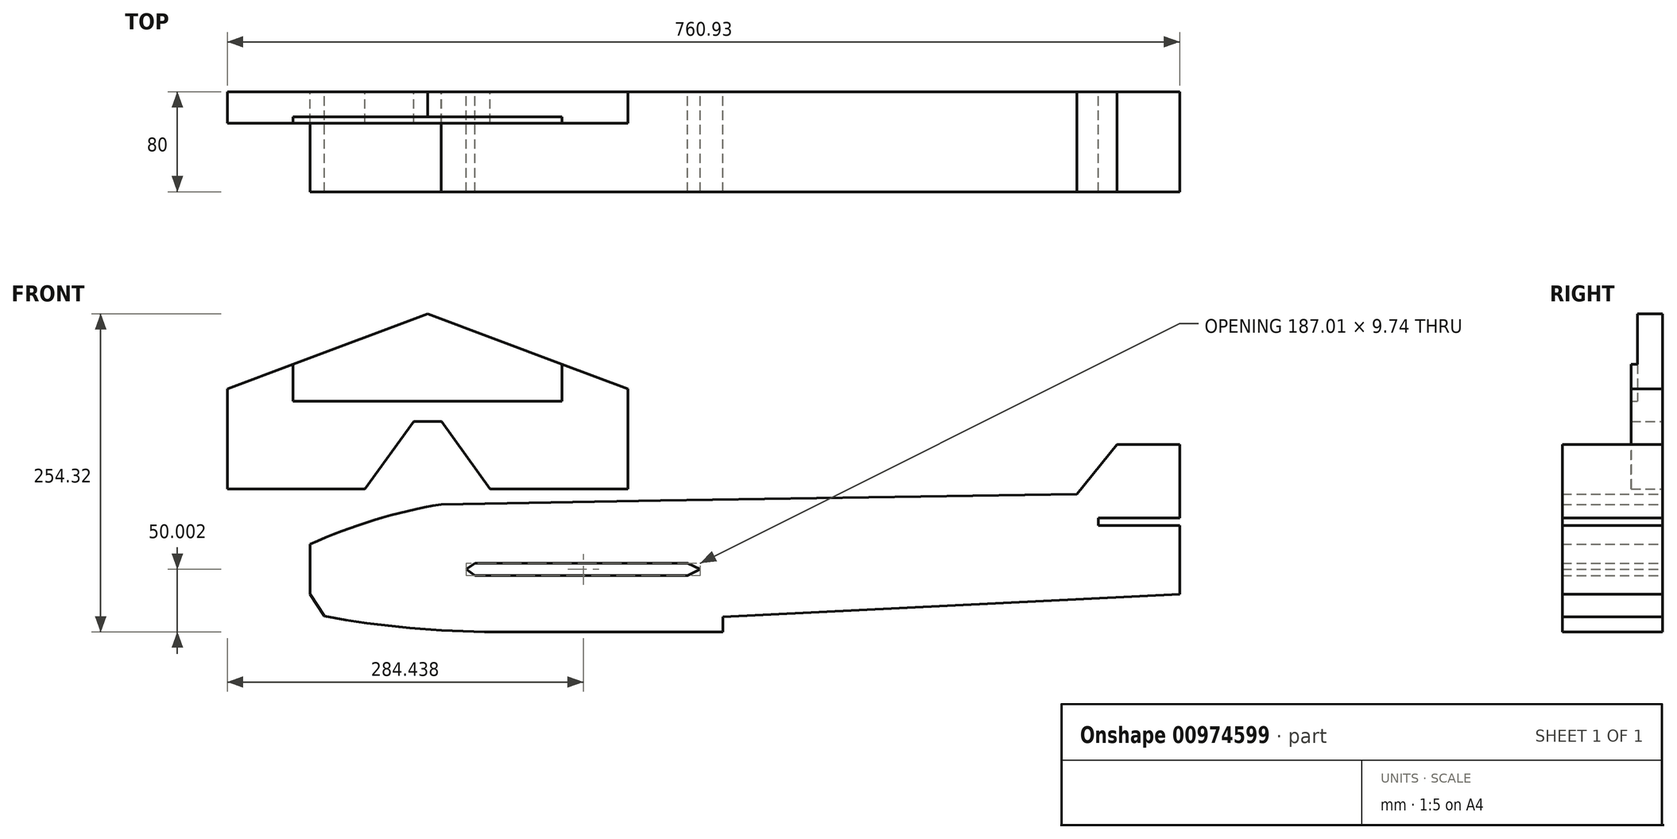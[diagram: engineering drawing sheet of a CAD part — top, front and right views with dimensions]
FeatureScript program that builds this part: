
annotation { "Feature Type Name" : "Feature", "Feature Type Description" : "" }
export const myFeature = defineFeature(function(context is Context, id is Id, definition is map)
    precondition{}
    {
        {
            var Q0;
            Q0=qCreatedBy(makeId("Front.planeOp"),FACE);
            var sketch = newSketch(context, id + "F0", { "sketchPlane" : qUnion([Q0])});
            skLineSegment(sketch, "E0", {"start": v(-94.07, 15.13) * mm, "end": v(-94.07, -24.87) * mm});
            skLineSegment(sketch, "E1", {"start": v(-94.07, 15.13) * mm, "end": v(10.93, 47.13) * mm});
            skLineSegment(sketch, "E2", {"start": v(-94.07, -24.87) * mm, "end": v(-74.07, -54.87) * mm});
            skLineSegment(sketch, "E3", {"start": v(-74.07, -54.87) * mm, "end": v(235.93, -54.87) * mm});
            skLineSegment(sketch, "E4", {"start": v(10.93, 47.13) * mm, "end": v(185.93, 50.13) * mm});
            skLineSegment(sketch, "E5", {"start": v(235.93, -54.87) * mm, "end": v(235.93, -42.87) * mm});
            skLineSegment(sketch, "E6", {"start": v(235.93, -42.87) * mm, "end": v(600.93, -24.87) * mm});
            skLineSegment(sketch, "E7", {"start": v(600.93, -24.87) * mm, "end": v(600.93, 95.13) * mm});
            skLineSegment(sketch, "E8", {"start": v(600.93, 95.13) * mm, "end": v(550.93, 95.13) * mm});
            skLineSegment(sketch, "E9", {"start": v(550.93, 95.13) * mm, "end": v(518.93, 55.13) * mm});
            skLineSegment(sketch, "E10", {"start": v(518.93, 55.13) * mm, "end": v(185.93, 50.13) * mm});
            skLineSegment(sketch, "E11", {"start": v(600.93, 30.13) * mm, "end": v(535.93, 30.13) * mm});
            skLineSegment(sketch, "E12", {"start": v(535.93, 30.13) * mm, "end": v(535.93, 36.13) * mm});
            skLineSegment(sketch, "E13", {"start": v(535.93, 36.13) * mm, "end": v(600.93, 36.13) * mm});
            skArc(sketch, "E14", {"start": v(-82.43, -42.33) * mm, "mid": v(-13.64, -51.76) * mm, "end": v(55.72, -54.87) * mm});
            skArc(sketch, "E15", {"start": v(10.93, 47.13) * mm, "mid": v(-42.61, 34.57) * mm, "end": v(-94.07, 15.13) * mm});
            skLineSegment(sketch, "E16", {"start": v(-94.07, -4.87) * mm, "end": v(222.18, -4.87) * mm, "construction": true});
            skLineSegment(sketch, "E17", {"start": v(30.93, -4.87) * mm, "end": v(37.69, 0) * mm});
            skLineSegment(sketch, "E18", {"start": v(37.69, 0) * mm, "end": v(207.62, 0) * mm});
            skLineSegment(sketch, "E19", {"start": v(207.62, 0) * mm, "end": v(217.94, -4.87) * mm});
            skLineSegment(sketch, "E20.MirrorCS", {"start": v(37.69, -9.74) * mm, "end": v(207.62, -9.74) * mm});
            skLineSegment(sketch, "E21.MirrorCS", {"start": v(30.93, -4.87) * mm, "end": v(37.69, -9.74) * mm});
            skLineSegment(sketch, "E22.MirrorCS", {"start": v(207.62, -9.74) * mm, "end": v(217.94, -4.87) * mm});
            skSolve(sketch);
        }
        {
            var Q0;
            Q0=makeQuery(id+"F0.imprint","IMPRINT",FACE,{"disambiguationData":[TD([[makeQuery(id+"F0.imprint","IMPRINT",EDGE,{"derivedFrom":sQuery(id+"F0.wireOp",EDGE,"E0")}),1.0]])]});
            var Q1;
            Q1=makeQuery(id+"F0.imprint","IMPRINT",FACE,{"disambiguationData":[TD([[makeQuery(id+"F0.imprint","IMPRINT",EDGE,{"derivedFrom":sQuery(id+"F0.wireOp",EDGE,"E1")}),1.0]])]});
            extrude(context, id + "F1", {"entities" : qUnion([Q0, Q1]), "depth" : 80 * mm, "offsetDistance" : 25 * mm});
        }
        {
            var Q0;
            Q0=qCreatedBy(makeId("Front.planeOp"),FACE);
            var sketch = newSketch(context, id + "F2", { "sketchPlane" : qUnion([Q0])});
            skLineSegment(sketch, "E23", {"start": v(0, 113.45) * mm, "end": v(-11, 113.45) * mm});
            skLineSegment(sketch, "E24", {"start": v(-11, 113.45) * mm, "end": v(-50, 59.45) * mm});
            skLineSegment(sketch, "E25", {"start": v(-50, 59.45) * mm, "end": v(-160, 59.45) * mm});
            skLineSegment(sketch, "E26", {"start": v(-160, 59.45) * mm, "end": v(-160, 139.45) * mm});
            skLineSegment(sketch, "E27", {"start": v(-160, 139.45) * mm, "end": v(0, 199.45) * mm});
            skLineSegment(sketch, "E28", {"start": v(-107.5, 159.14) * mm, "end": v(-107.5, 129.45) * mm});
            skLineSegment(sketch, "E29", {"start": v(-107.5, 129.45) * mm, "end": v(0, 129.45) * mm});
            skLineSegment(sketch, "E30.MirrorCS", {"start": v(160, 139.45) * mm, "end": v(0, 199.45) * mm});
            skLineSegment(sketch, "E31.MirrorCS", {"start": v(160, 59.45) * mm, "end": v(160, 139.45) * mm});
            skLineSegment(sketch, "E32.MirrorCS", {"start": v(50, 59.45) * mm, "end": v(160, 59.45) * mm});
            skLineSegment(sketch, "E33.MirrorCS", {"start": v(11, 113.45) * mm, "end": v(50, 59.45) * mm});
            skLineSegment(sketch, "E34.MirrorCS", {"start": v(0, 113.45) * mm, "end": v(11, 113.45) * mm});
            skLineSegment(sketch, "E35.MirrorCS", {"start": v(107.5, 129.45) * mm, "end": v(0, 129.45) * mm});
            skLineSegment(sketch, "E36.MirrorCS", {"start": v(107.5, 159.14) * mm, "end": v(107.5, 129.45) * mm});
            skSolve(sketch);
        }
        {
            var Q0;
            Q0=makeQuery(id+"F2.imprint","IMPRINT",FACE,{"disambiguationData":[TD([[makeQuery(id+"F2.imprint","IMPRINT",EDGE,{"derivedFrom":sQuery(id+"F2.wireOp",EDGE,"E23")}),-1.0]])]});
            extrude(context, id + "F3", {"entities" : qUnion([Q0]), "depth" : 25 * mm, "offsetDistance" : 25 * mm});
        }
        {
            var Q0;
            {var subQ4=sQuery(id+"F2.wireOp",EDGE,"E28");Q0=makeQuery(id+"F2.imprint","IMPRINT",FACE,{"disambiguationData":[TD([[makeQuery(id+"F2.imprint","IMPRINT",EDGE,{"derivedFrom":subQ4}),1.0]])]});}
            extrude(context, id + "F4", {"entities" : qUnion([Q0]), "operationType" : NewBodyOperationType.ADD, "depth" : 20 * mm, "offsetDistance" : 25 * mm});
        }
    });
